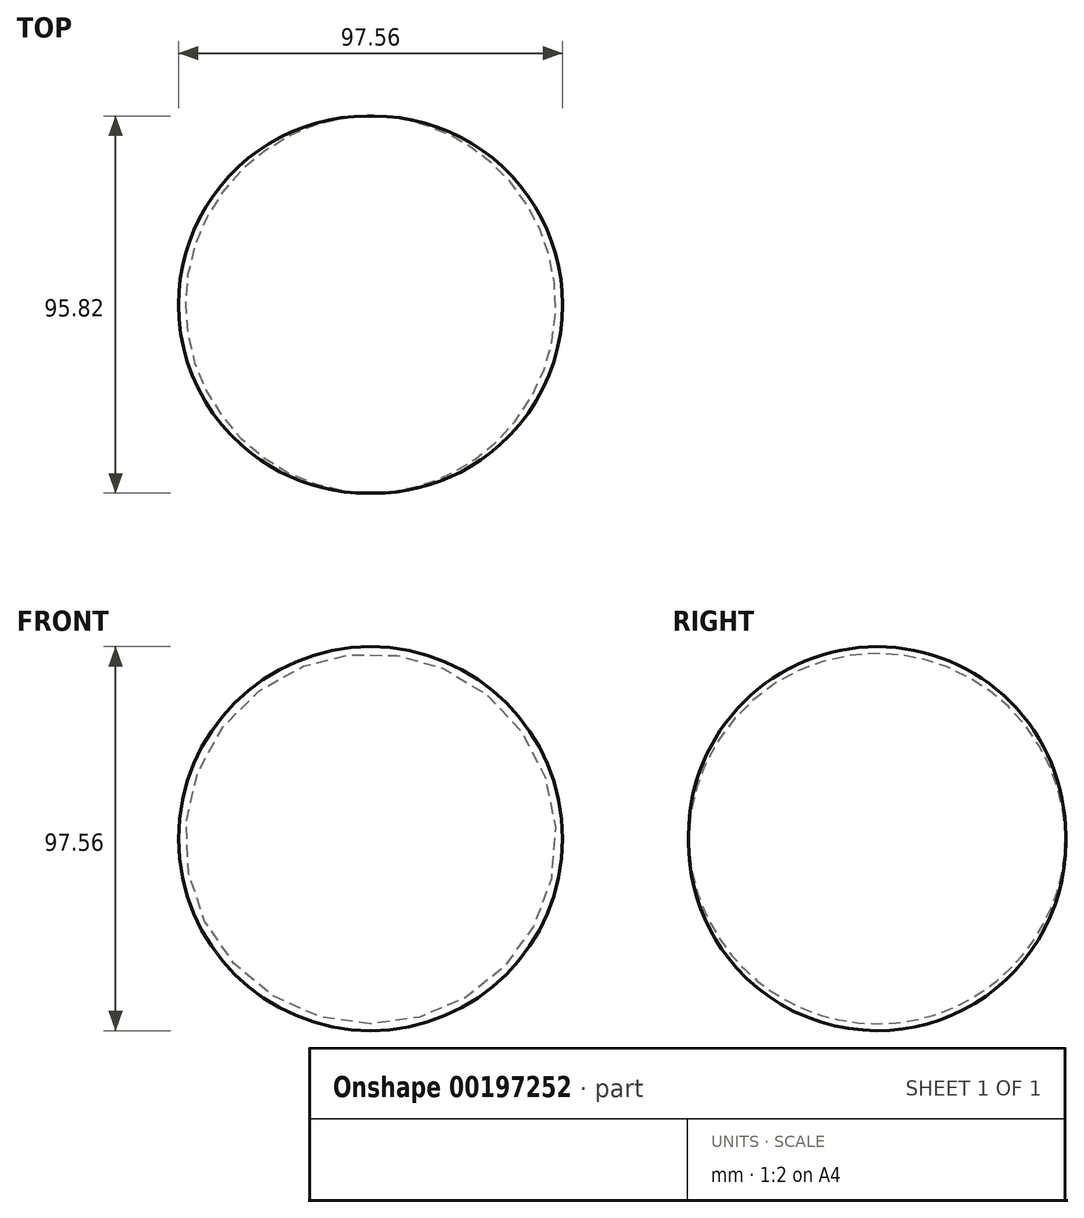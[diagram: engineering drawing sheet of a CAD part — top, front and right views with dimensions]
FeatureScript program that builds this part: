
annotation { "Feature Type Name" : "Feature", "Feature Type Description" : "" }
export const myFeature = defineFeature(function(context is Context, id is Id, definition is map)
    precondition{}
    {
        {
            var Q0;
            Q0=qCreatedBy(makeId("Top.planeOp"),FACE);
            var sketch = newSketch(context, id + "F0", { "sketchPlane" : qUnion([Q0])});
            skArc(sketch, "E0", {"start": v(0, 39.96) * mm, "mid": v(-47.04, -7.94) * mm, "end": v(0, -55.84) * mm});
            skLineSegment(sketch, "E1", {"start": v(0, 39.96) * mm, "end": v(0, -55.84) * mm});
            skSolve(sketch);
        }
        {
            var Q0;
            Q0 = qSketchRegion(id + "F0", true);
            var Q1;
            Q1=sQuery(id+"F0.wireOp",EDGE,"E1");
            revolve(context, id + "F1", {"entities" : qUnion([Q0]), "axis" : qUnion([Q1]), "revolveType" : RevolveType.FULL});
        }
    });
